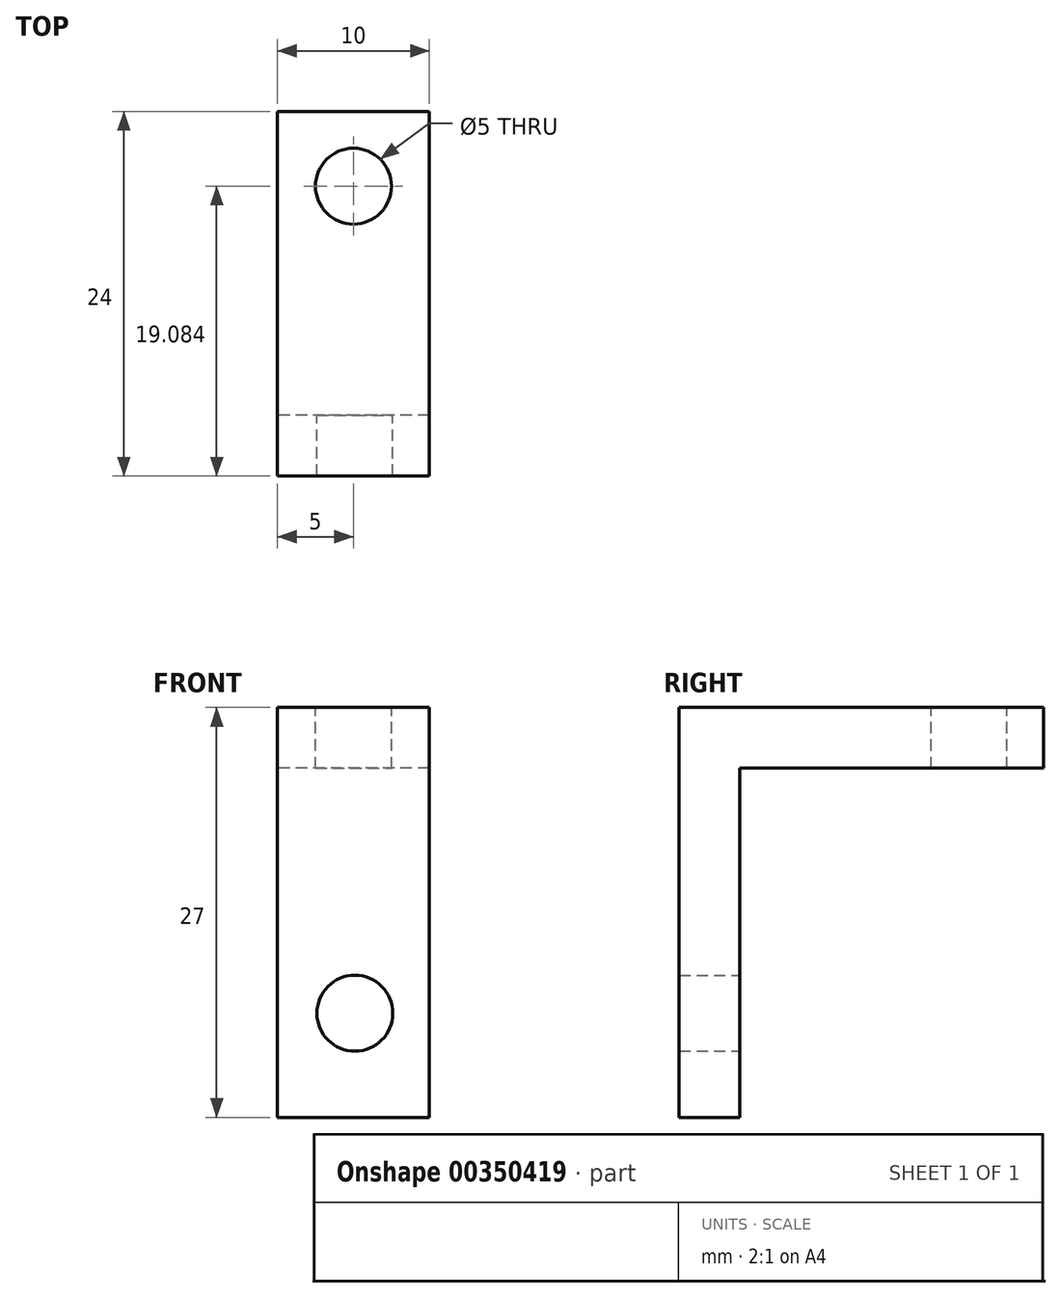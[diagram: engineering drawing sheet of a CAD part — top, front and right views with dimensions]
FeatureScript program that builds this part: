
annotation { "Feature Type Name" : "Feature", "Feature Type Description" : "" }
export const myFeature = defineFeature(function(context is Context, id is Id, definition is map)
    precondition{}
    {
        {
            var Q0;
            Q0=qCreatedBy(makeId("Right.planeOp"),FACE);
            var sketch = newSketch(context, id + "F0", { "sketchPlane" : qUnion([Q0])});
            skLineSegment(sketch, "E0", {"start": v(0, 0) * mm, "end": v(-4, 0) * mm});
            skLineSegment(sketch, "E1", {"start": v(-4, 0) * mm, "end": v(-4, 27) * mm});
            skLineSegment(sketch, "E2", {"start": v(-4, 27) * mm, "end": v(20, 27) * mm});
            skLineSegment(sketch, "E3", {"start": v(20, 27) * mm, "end": v(20, 23) * mm});
            skLineSegment(sketch, "E4", {"start": v(20, 23) * mm, "end": v(0, 23) * mm});
            skLineSegment(sketch, "E5", {"start": v(0, 23) * mm, "end": v(0, 0) * mm});
            skSolve(sketch);
        }
        {
            var Q0;
            Q0 = qSketchRegion(id + "F0", true);
            extrude(context, id + "F1", {"entities" : qUnion([Q0]), "depth" : 10 * mm});
        }
        {
            var Q0;
            Q0=makeQuery(id+"F1.opExtrude","SWEPT_FACE",FACE,{"disambiguationData":[OSD([sQuery(id+"F0.wireOp",EDGE,"E5")])]});
            var sketch = newSketch(context, id + "F2", { "sketchPlane" : qUnion([Q0])});
            skCircle(sketch, "E6", {"center": v(-5.1, 6.86) * mm, "radius": 2.5 * mm});
            skSolve(sketch);
        }
        {
            var Q0;
            Q0 = qSketchRegion(id + "F2", true);
            extrude(context, id + "F3", {"entities" : qUnion([Q0]), "operationType" : NewBodyOperationType.REMOVE, "oppositeDirection" : true, "depth" : 25 * mm});
        }
        {
            var Q0;
            Q0=makeQuery(id+"F1.opExtrude","SWEPT_FACE",FACE,{"disambiguationData":[OSD([sQuery(id+"F0.wireOp",EDGE,"E2")])]});
            var sketch = newSketch(context, id + "F4", { "sketchPlane" : qUnion([Q0])});
            skCircle(sketch, "E7", {"center": v(5, 15.08) * mm, "radius": 2.5 * mm});
            skPoint(sketch, "E7.centerSnap0", {"position": v(5, 20) * mm});
            skSolve(sketch);
        }
        {
            var Q0;
            Q0 = qSketchRegion(id + "F4", true);
            extrude(context, id + "F5", {"entities" : qUnion([Q0]), "operationType" : NewBodyOperationType.REMOVE, "oppositeDirection" : true, "depth" : 36.2 * mm});
        }
    });
